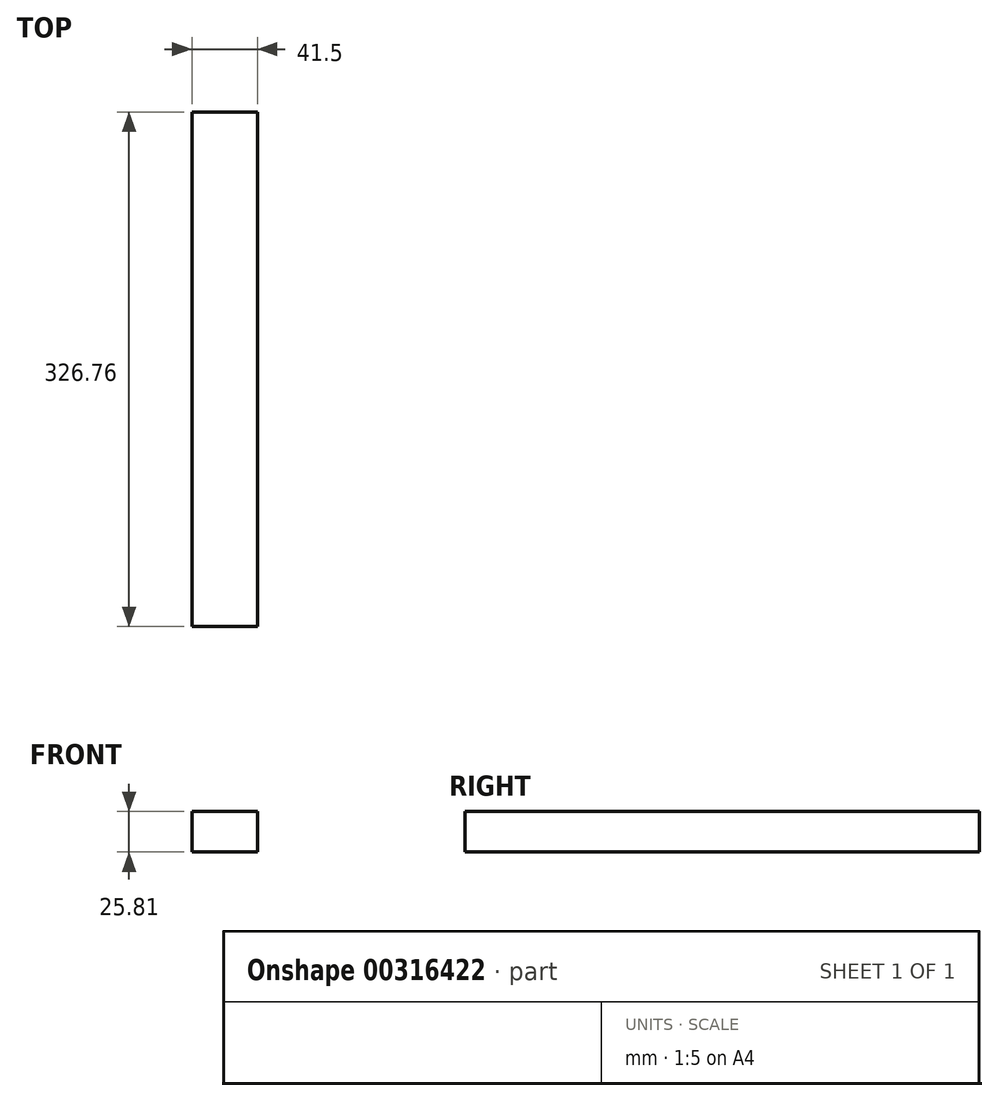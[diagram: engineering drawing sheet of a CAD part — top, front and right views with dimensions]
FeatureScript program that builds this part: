
annotation { "Feature Type Name" : "Feature", "Feature Type Description" : "" }
export const myFeature = defineFeature(function(context is Context, id is Id, definition is map)
    precondition{}
    {
        {
            var Q0;
            Q0=qCreatedBy(makeId("Front.planeOp"),FACE);
            var sketch = newSketch(context, id + "F0", { "sketchPlane" : qUnion([Q0])});
            skLineSegment(sketch, "E0.bottom", {"start": v(0, 24) * mm, "end": v(41.5, 24) * mm});
            skLineSegment(sketch, "E0.top", {"start": v(0, 49.82) * mm, "end": v(41.5, 49.82) * mm});
            skLineSegment(sketch, "E0.left", {"start": v(0, 24) * mm, "end": v(0, 49.82) * mm});
            skLineSegment(sketch, "E0.right", {"start": v(41.5, 24) * mm, "end": v(41.5, 49.82) * mm});
            skSolve(sketch);
        }
        {
            var Q0;
            Q0=makeQuery(id+"F0.imprint","IMPRINT",FACE,{"disambiguationData":[TD([[makeQuery(id+"F0.imprint","IMPRINT",EDGE,{"derivedFrom":sQuery(id+"F0.wireOp",EDGE,"E0.bottom")}),1.0]])]});
            extrude(context, id + "F1", {"entities" : qUnion([Q0]), "depth" : 326.76 * mm});
        }
    });
